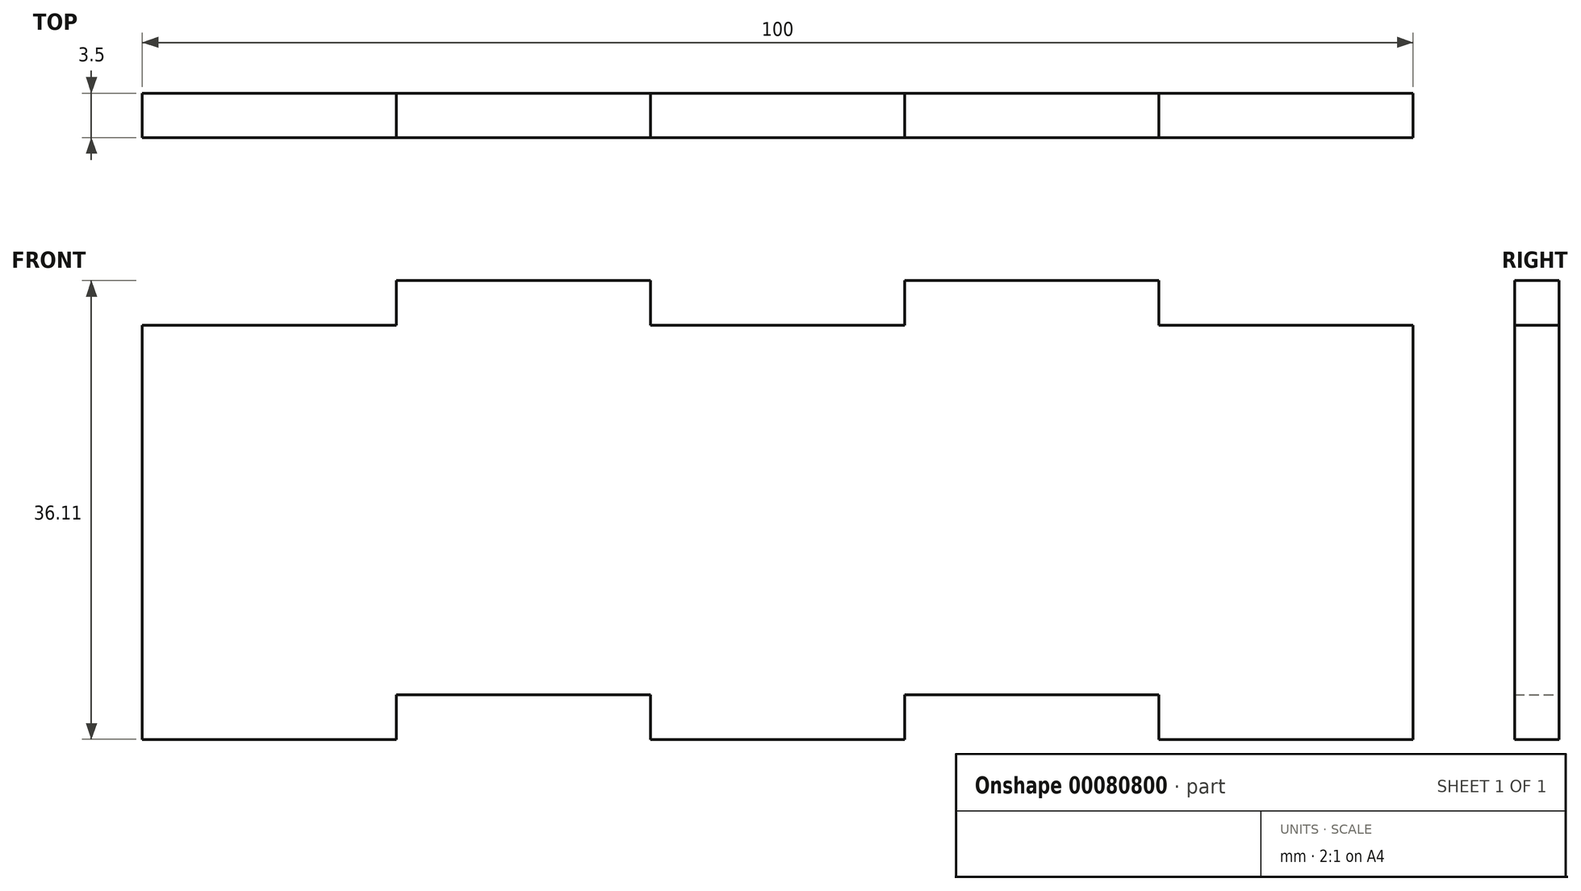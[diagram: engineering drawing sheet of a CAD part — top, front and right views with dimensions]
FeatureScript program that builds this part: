
annotation { "Feature Type Name" : "Feature", "Feature Type Description" : "" }
export const myFeature = defineFeature(function(context is Context, id is Id, definition is map)
    precondition{}
    {
        {
            var Q0;
            Q0=qCreatedBy(makeId("Front.planeOp"),FACE);
            var sketch = newSketch(context, id + "F0", { "sketchPlane" : qUnion([Q0])});
            skLineSegment(sketch, "E0.bottom", {"start": v(-60, -61.97) * mm, "end": v(40, -61.97) * mm});
            skLineSegment(sketch, "E0.top", {"start": v(-60, -98.08) * mm, "end": v(40, -98.08) * mm});
            skLineSegment(sketch, "E0.left", {"start": v(-60, -61.97) * mm, "end": v(-60, -98.08) * mm});
            skLineSegment(sketch, "E0.right", {"start": v(40, -61.97) * mm, "end": v(40, -98.08) * mm});
            skLineSegment(sketch, "E1.direction1", {"start": v(-60, -98.08) * mm, "end": v(-49.65, -98.08) * mm, "construction": true});
            skLineSegment(sketch, "E2", {"start": v(-40, -98.08) * mm, "end": v(-40, -94.58) * mm});
            skLineSegment(sketch, "E3", {"start": v(-40, -94.58) * mm, "end": v(-20, -94.58) * mm});
            skLineSegment(sketch, "E4", {"start": v(-20, -94.58) * mm, "end": v(-20, -98.08) * mm});
            skLineSegment(sketch, "E5", {"start": v(-20, -98.08) * mm, "end": v(0, -98.08) * mm});
            skLineSegment(sketch, "E6", {"start": v(0, -98.08) * mm, "end": v(0, -94.58) * mm});
            skLineSegment(sketch, "E7", {"start": v(-60, -98.08) * mm, "end": v(-40, -98.08) * mm});
            skLineSegment(sketch, "E8", {"start": v(0, -94.58) * mm, "end": v(20, -94.58) * mm});
            skLineSegment(sketch, "E9", {"start": v(20, -94.58) * mm, "end": v(20, -98.08) * mm});
            skLineSegment(sketch, "E10", {"start": v(-60, -65.47) * mm, "end": v(-40, -65.47) * mm});
            skLineSegment(sketch, "E11", {"start": v(-40, -65.47) * mm, "end": v(-40, -61.97) * mm});
            skLineSegment(sketch, "E12", {"start": v(-40, -61.97) * mm, "end": v(-20, -61.97) * mm});
            skLineSegment(sketch, "E13", {"start": v(-20, -61.97) * mm, "end": v(-20, -65.47) * mm});
            skLineSegment(sketch, "E14", {"start": v(-20, -65.47) * mm, "end": v(0, -65.47) * mm});
            skLineSegment(sketch, "E15", {"start": v(0, -65.47) * mm, "end": v(0, -61.97) * mm});
            skLineSegment(sketch, "E16", {"start": v(0, -61.97) * mm, "end": v(20, -61.97) * mm});
            skLineSegment(sketch, "E17", {"start": v(20, -61.97) * mm, "end": v(20, -65.47) * mm});
            skLineSegment(sketch, "E18", {"start": v(20, -65.47) * mm, "end": v(40, -65.47) * mm});
            skSolve(sketch);
        }
        {
            var Q0;
            Q0=makeQuery(id+"F0.imprint","IMPRINT",FACE,{"disambiguationData":[TD([[makeQuery(id+"F0.imprint","IMPRINT",EDGE,{"derivedFrom":sQuery(id+"F0.wireOp",EDGE,"E2")}),1.0]])]});
            extrude(context, id + "F1", {"entities" : qUnion([Q0]), "depth" : 3.5 * mm});
        }
    });
